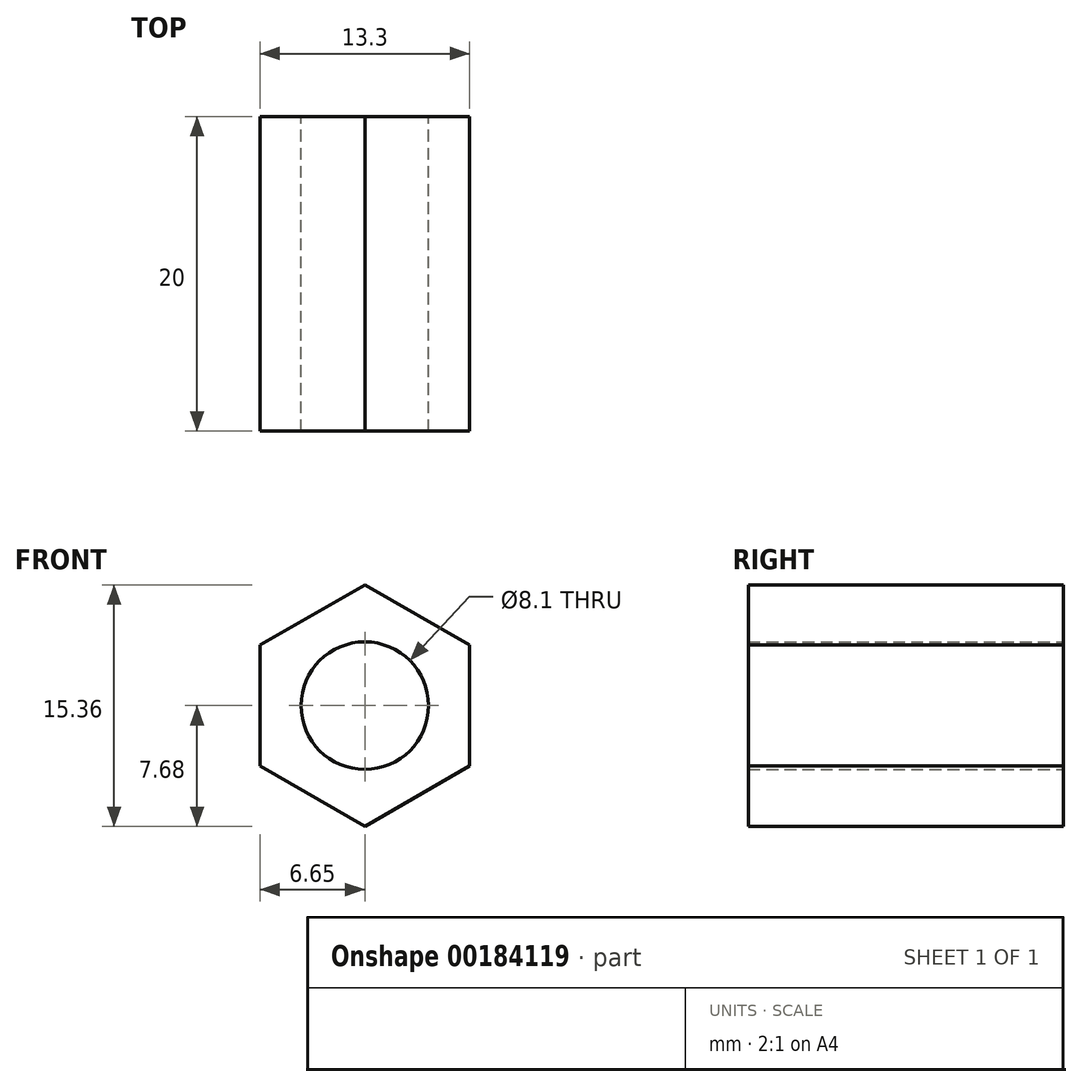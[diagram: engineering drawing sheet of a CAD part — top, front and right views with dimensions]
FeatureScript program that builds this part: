
annotation { "Feature Type Name" : "Feature", "Feature Type Description" : "" }
export const myFeature = defineFeature(function(context is Context, id is Id, definition is map)
    precondition{}
    {
        {
            var Q0;
            Q0=qCreatedBy(makeId("Front.planeOp"),FACE);
            var sketch = newSketch(context, id + "F0", { "sketchPlane" : qUnion([Q0])});
            skCircle(sketch, "E0.cCircle", {"center": v(0, 0) * mm, "radius": 6.65 * mm, "construction": true});
            skLineSegment(sketch, "E0.0", {"start": v(0, 7.68) * mm, "end": v(6.65, 3.84) * mm});
            skLineSegment(sketch, "E0.1", {"start": v(6.65, 3.84) * mm, "end": v(6.65, -3.84) * mm});
            skLineSegment(sketch, "E0.2", {"start": v(6.65, -3.84) * mm, "end": v(0, -7.68) * mm});
            skLineSegment(sketch, "E0.3", {"start": v(0, -7.68) * mm, "end": v(-6.65, -3.84) * mm});
            skLineSegment(sketch, "E0.4", {"start": v(-6.65, -3.84) * mm, "end": v(-6.65, 3.84) * mm});
            skLineSegment(sketch, "E0.5", {"start": v(-6.65, 3.84) * mm, "end": v(0, 7.68) * mm});
            skPoint(sketch, "E0.0.midPoint", {"position": v(3.33, 5.76) * mm});
            skCircle(sketch, "E1.cCircle", {"center": v(0, 0) * mm, "radius": 6.65 * mm});
            skPoint(sketch, "E1.0.midPoint", {"position": v(-3.32, 5.76) * mm});
            skCircle(sketch, "E2", {"center": v(0, 0) * mm, "radius": 4.05 * mm});
            skSolve(sketch);
        }
        {
            var Q0;
            Q0 = qSketchRegion(id + "F0", true);
            extrude(context, id + "F1", {"entities" : qUnion([Q0]), "depth" : 20 * mm});
        }
    });
